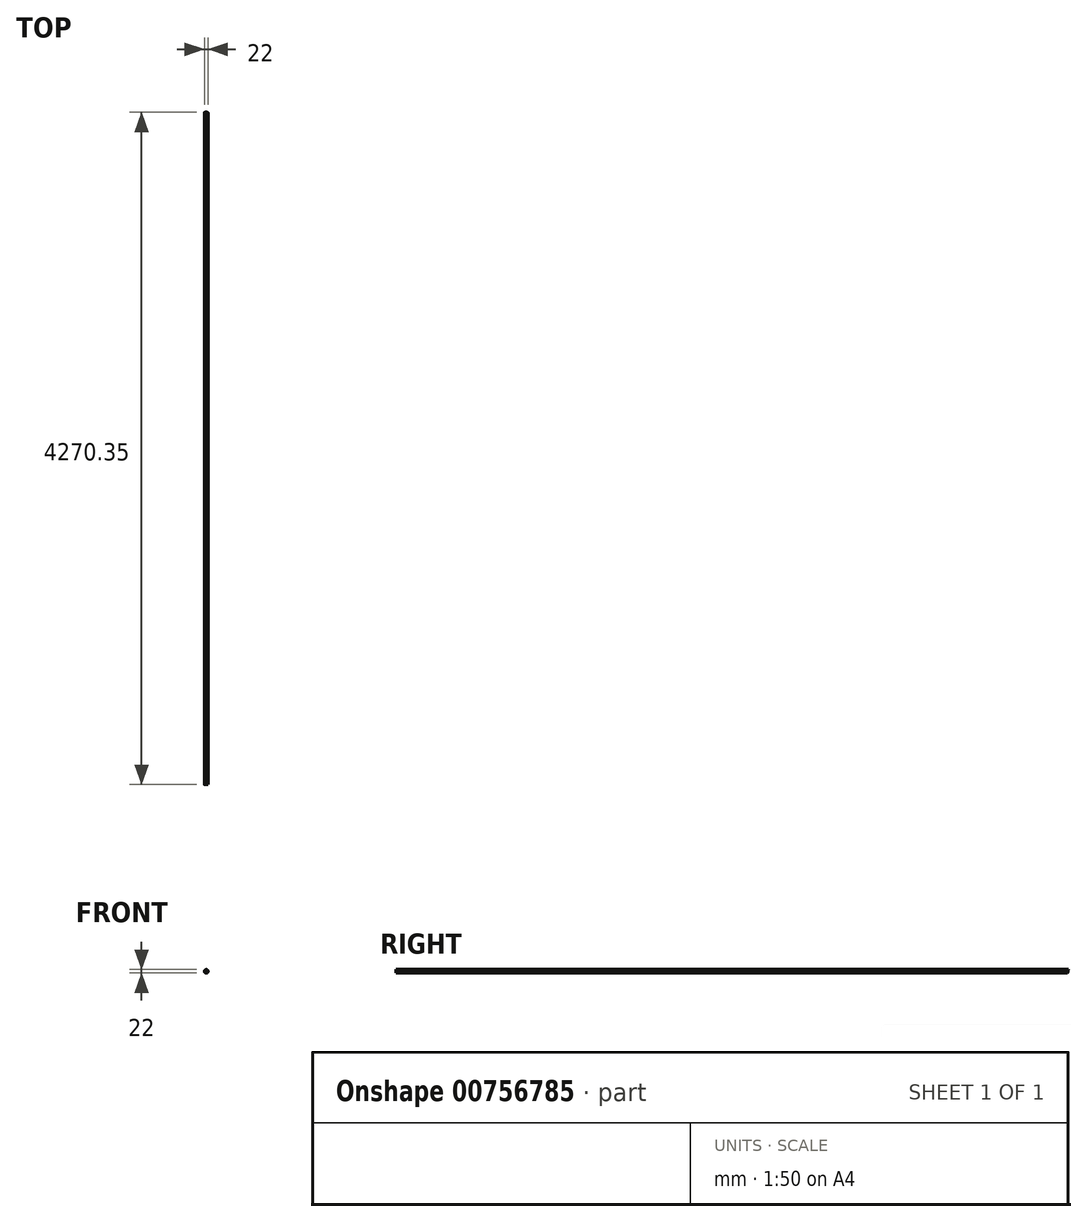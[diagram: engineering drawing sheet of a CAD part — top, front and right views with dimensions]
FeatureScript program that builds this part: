
annotation { "Feature Type Name" : "Feature", "Feature Type Description" : "" }
export const myFeature = defineFeature(function(context is Context, id is Id, definition is map)
    precondition{}
    {
        {
            var Q0;
            Q0=qCreatedBy(makeId("Front.planeOp"),FACE);
            var sketch = newSketch(context, id + "F0", { "sketchPlane" : qUnion([Q0])});
            skCircle(sketch, "E0", {"center": v(0, 0) * mm, "radius": 11 * mm});
            skSolve(sketch);
        }
        {
            var Q0;
            Q0=makeQuery(id+"F0.imprint","IMPRINT",FACE,{"disambiguationData":[TD([[makeQuery(id+"F0.imprint","IMPRINT",EDGE,{"derivedFrom":sQuery(id+"F0.wireOp",EDGE,"E0")}),1.0]])]});
            extrude(context, id + "F1", {"entities" : qUnion([Q0]), "depth" : 4270.35 * mm, "offsetDistance" : 25 * mm});
        }
        {
            var Q0;
            Q0=qCreatedBy(makeId("Right.planeOp"),FACE);
            var sketch = newSketch(context, id + "F2", { "sketchPlane" : qUnion([Q0])});
            skLineSegment(sketch, "E1.0", {"start": v(0, -11) * mm, "end": v(0, 11) * mm});
            skLineSegment(sketch, "E2", {"start": v(0, -11) * mm, "end": v(-4270.35, -11) * mm});
            skLineSegment(sketch, "E3", {"start": v(0, 11) * mm, "end": v(-3.88, -11) * mm});
            skSolve(sketch);
        }
        {
            var Q0;
            Q0 = qSketchRegion(id + "F2", true);
            extrude(context, id + "F3", {"entities" : qUnion([Q0]), "operationType" : NewBodyOperationType.REMOVE, "endBound" : BoundingType.SYMMETRIC, "depth" : 50 * mm, "offsetDistance" : 25 * mm});
        }
    });
